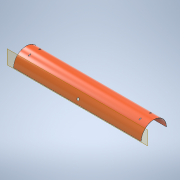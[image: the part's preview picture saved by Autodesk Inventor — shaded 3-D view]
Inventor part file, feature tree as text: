
AUTODESK INVENTOR PART (.ipt)
format: ipt  version: 2022 (Build 260153000, 153)  size: 150,016 bytes
history: native  units: mm
features: sketch x3, hole x2, extrude x1, plane x1, projected_geometry x1
ambient origin geometry x8: Origin, YZ Plane, XZ Plane, XY Plane, X Axis, Y Axis, Z Axis, Center Point
bodies: Solid1 (feature_tree)
feature tree (8):
  extrude  "Extrusion1"  Depth=59.6mm
  hole  "Hole1"  [1 undecoded]
  plane  "Work Plane1"
  hole  "Hole2"  [1 undecoded]
  sketch  "Sketch1"  dims[d0=29.8mm d1=59.6mm]
  sketch  "Sketch2"  dims[d4=29.48mm d5=300.0mm d6=0.0mm]
  projected_geometry  "Projected Loop1"
  sketch  "Sketch3"  dims[d7=10.0mm d8=5.4mm d9=6.0mm d10=4.0mm d11=2.0mm d12=90.0deg d13=8.0mm d14=20.594885mm d16=20.0mm d17=27.0mm d19=260.0mm d20=2.0mm d21=6.0mm d22=4.0mm d23=2.0mm d24=90.0deg d25=8.0mm d26=20.594885mm]
note: 2 required parameter values undecoded (feature->parameter linkage not recoverable at this tier; creation-order binding heuristic only, values carry confidence <= 0.55)
